# Revit family: 84
name_source: partatom
category: Instalační zařizovací předměty
revit_build: Autodesk Revit 2016 (Build: 20161004_0715(x64)
units: mm (PartAtom-declared; Revit-internal decimal feet)

## family parameters
Bod výpočtu místnosti = Ano
Kóta kulaté spojky = Použít průměr
Nadpis OmniClass = Deck Waste Water Drains
Ořezat dutým tvarem při načtení = Ne
Sdílené = Ne
Typ součásti = Normální
Vždy vertikální = Ano
Založené na pracovní rovině = Ne
Číslo OmniClass = 23.70.50.21.24.14

## types (3) — shared parameters
BUILD-IN HEIGHT = 16 mm
Klíčová poznámka = 84
MATERIAL = PP
Model = 84
Popis = Roof drains
Připojení CW = Ne
Připojení HW = Ne
Připojení odpadu = Ano
Připojení ventilace = Ne
URL = http://www.dallmer.com
Výrobce = Dallmer Ltd.

## per-type parameters (varying)
| type | CAPACITY | DIMENSION | GTIN | Komentáře k typům | NOMINAL DIAMETER | WEIGHT |
| 84.1026 | 5,79 | DN 50 | 4001636831026 | balcony drain body type 84, DN 50 | 50 mm | 0,43 |
| 84.1040 | 6,14 | DN 70 | 4001636831040 | balcony drain body type 84, DN 70 | 70 mm | 0,46 |
| 84.1064 | 5,62 | DN 100 | 4001636831064 | balcony drain body type 84, DN 100 | 100 mm | 0,78 |

## geometry (parser evidence)
native form markers: Sweep x4
no freeform markers — native parametric forms only
